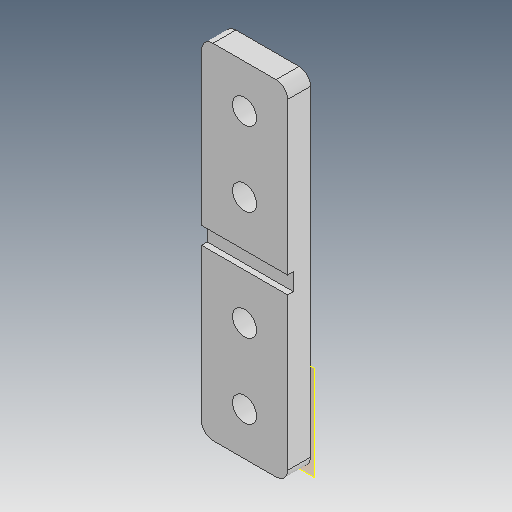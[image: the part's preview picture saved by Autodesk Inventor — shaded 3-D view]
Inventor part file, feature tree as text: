
AUTODESK INVENTOR PART (.ipt)
format: ipt  version: 2020 (Build 240168000, 168)  size: 134,656 bytes
history: native  units: mm
features: other x8, extrude x3, sketch x3
ambient origin geometry x8: Origin, YZ Plane, XZ Plane, XY Plane, X Axis, Y Axis, Z Axis, Center Point
bodies: Body1 (feature_tree)
feature tree (14):
  other  "Sólido1"
  other  "Plano de trabalho1"
  extrude  "Extrusão1"  Depth=28.5mm
  extrude  "Extrusão2"  Depth=3.0mm
  extrude  "Extrusão3"  Depth=10.0mm
  sketch  "Esboço1"  dims[d0=4.0mm d1=0.0mm d4=28.5mm]
  other  "Referência1"
  other  "Referência2"
  sketch  "Esboço2"  dims[d5=28.5mm d6=3.0mm]
  sketch  "Esboço3"  dims[d7=4.2mm d8=4.2mm d9=8.0mm d10=8.0mm d11=1.0mm d12=0.0mm d13=10.0mm d14=0.0mm]
  other  "<userpath>\OneDrive\Área de Trabalho\Calorimetro 2022\Inventor\Montagem_suporte_termopar.iam"
  other  "Montagem_suporte_termopar.iam"
  other  "suporte_termopar:1"
  other  "Montagem1"
